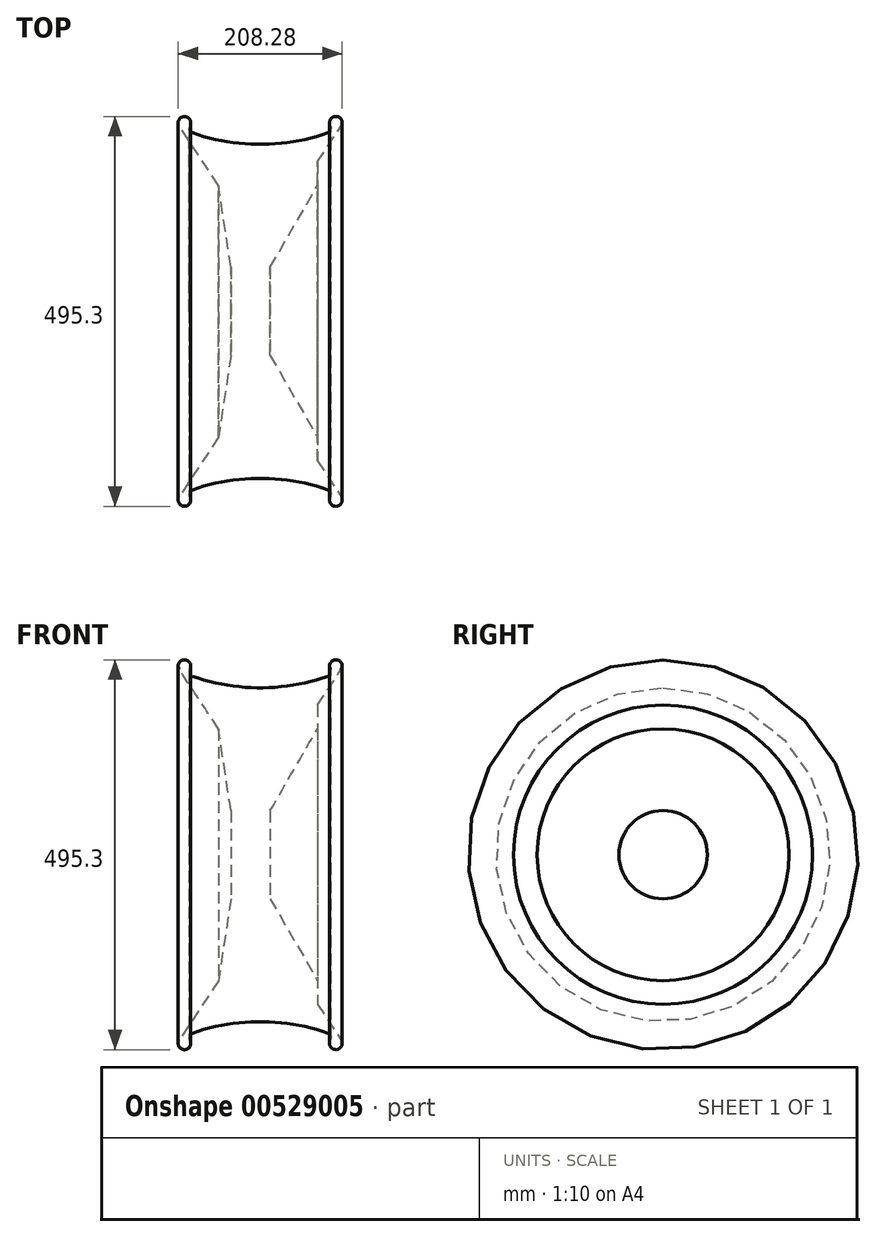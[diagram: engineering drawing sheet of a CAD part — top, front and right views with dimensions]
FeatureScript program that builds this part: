
annotation { "Feature Type Name" : "Feature", "Feature Type Description" : "" }
export const myFeature = defineFeature(function(context is Context, id is Id, definition is map)
    precondition{}
    {
        {
            var Q0;
            Q0=qCreatedBy(makeId("Front.planeOp"),FACE);
            var sketch = newSketch(context, id + "F0", { "sketchPlane" : qUnion([Q0])});
            skLineSegment(sketch, "E0", {"start": v(0, 0) * mm, "end": v(997.5, 0) * mm, "construction": true});
            skLineSegment(sketch, "E1", {"start": v(847.5, 0) * mm, "end": v(847.5, 56.08) * mm});
            skLineSegment(sketch, "E2", {"start": v(997.5, 247.65) * mm, "end": v(904.13, 247.65) * mm, "construction": true});
            skLineSegment(sketch, "E3", {"start": v(847.5, 56.08) * mm, "end": v(907.5, 160) * mm});
            skLineSegment(sketch, "E4", {"start": v(907.5, 160) * mm, "end": v(907.5, 190) * mm});
            skLineSegment(sketch, "E5", {"start": v(907.5, 190) * mm, "end": v(937.5, 235.23) * mm});
            skArc(sketch, "E6", {"start": v(937.5, 235.23) * mm, "mid": v(931, 247.65) * mm, "end": v(923.98, 235.52) * mm});
            skArc(sketch, "E7", {"start": v(923.98, 235.52) * mm, "mid": v(924.49, 230.4) * mm, "end": v(920.83, 226.76) * mm});
            skArc(sketch, "E8", {"start": v(920.83, 226.76) * mm, "mid": v(834.7, 212.08) * mm, "end": v(748.56, 226.76) * mm});
            skLineSegment(sketch, "E9", {"start": v(934.2, 244.73) * mm, "end": v(928.1, 235.52) * mm, "construction": true});
            skLineSegment(sketch, "E10", {"start": v(834.7, 509.65) * mm, "end": v(834.7, 212.08) * mm, "construction": true});
            skArc(sketch, "E11.MirrorCS", {"start": v(731.89, 235.23) * mm, "mid": v(738.38, 247.65) * mm, "end": v(745.4, 235.52) * mm});
            skArc(sketch, "E12.MirrorCS", {"start": v(745.4, 235.52) * mm, "mid": v(744.9, 230.4) * mm, "end": v(748.56, 226.76) * mm});
            skLineSegment(sketch, "E13", {"start": v(730.55, 253.46) * mm, "end": v(730.55, 221.68) * mm, "construction": true});
            skLineSegment(sketch, "E14", {"start": v(938.83, 256.83) * mm, "end": v(938.83, 212.62) * mm, "construction": true});
            skLineSegment(sketch, "E15", {"start": v(731.89, 235.23) * mm, "end": v(781.79, 160) * mm});
            skLineSegment(sketch, "E16", {"start": v(847.5, 0) * mm, "end": v(797.5, 0) * mm});
            skLineSegment(sketch, "E17", {"start": v(797.5, 0) * mm, "end": v(797.5, 56.08) * mm});
            skLineSegment(sketch, "E18", {"start": v(781.79, 160) * mm, "end": v(797.5, 56.08) * mm});
            skSolve(sketch);
        }
        {
            var Q0;
            Q0=makeQuery(id+"F0.imprint","IMPRINT",FACE,{"disambiguationData":[TD([[makeQuery(id+"F0.imprint","IMPRINT",EDGE,{"derivedFrom":sQuery(id+"F0.wireOp",EDGE,"E1")}),1.0]])]});
            var Q1;
            Q1=sQuery(id+"F0.wireOp",EDGE,"E0");
            revolve(context, id + "F1", {"entities" : qUnion([Q0]), "axis" : qUnion([Q1]), "revolveType" : RevolveType.FULL});
        }
    });
